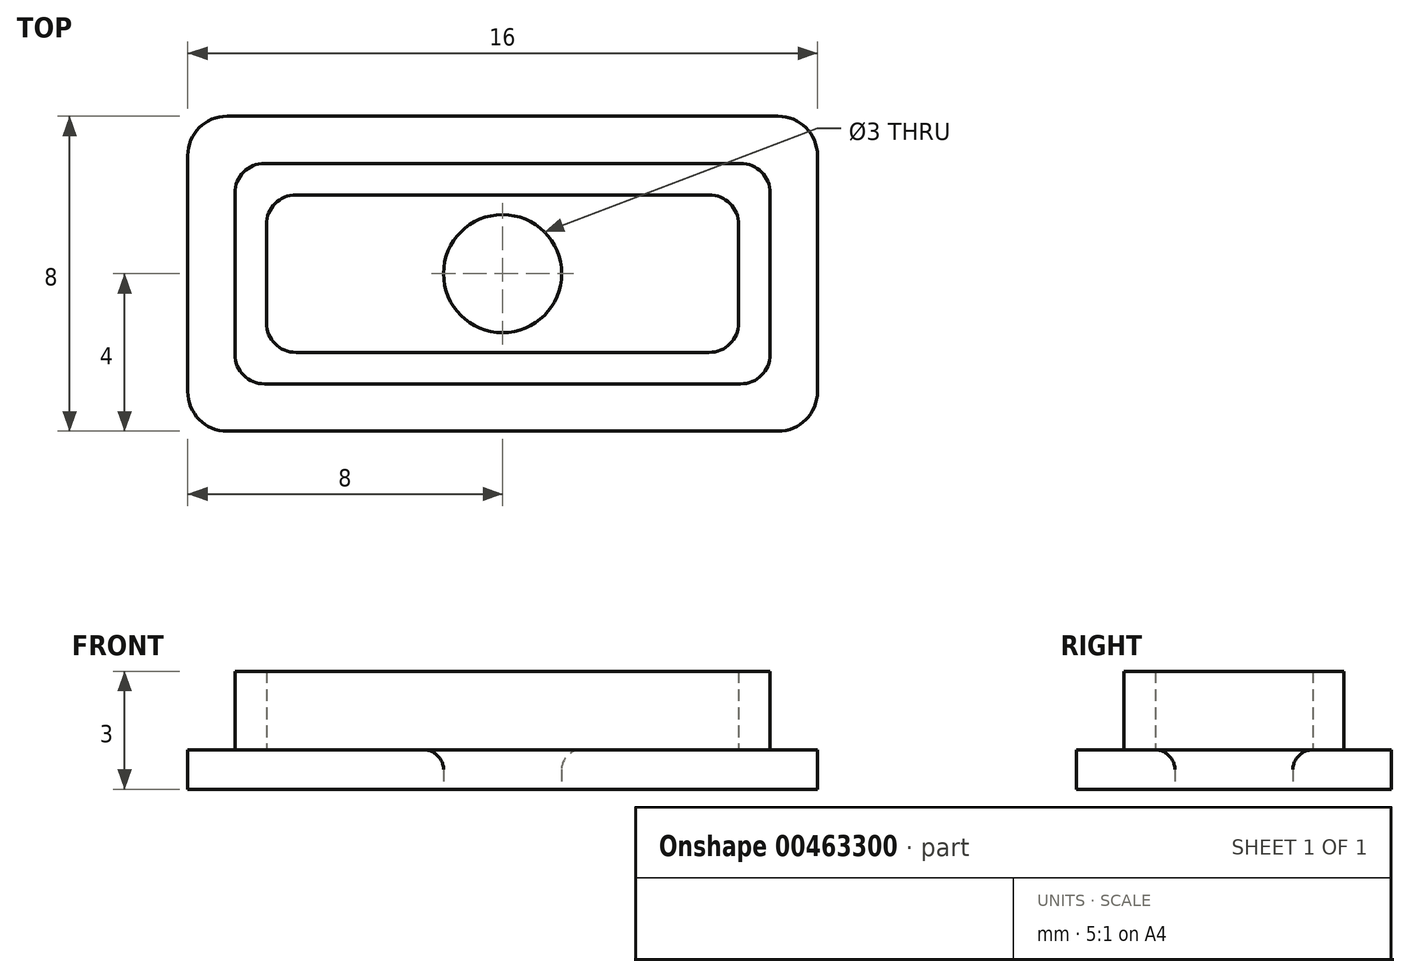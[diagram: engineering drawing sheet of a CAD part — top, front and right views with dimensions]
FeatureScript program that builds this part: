
annotation { "Feature Type Name" : "Feature", "Feature Type Description" : "" }
export const myFeature = defineFeature(function(context is Context, id is Id, definition is map)
    precondition{}
    {
        {
            var Q0;
            Q0=qCreatedBy(makeId("Top.planeOp"),FACE);
            var sketch = newSketch(context, id + "F0", { "sketchPlane" : qUnion([Q0])});
            skLineSegment(sketch, "E0.bottom", {"start": v(6.8, -2.8) * mm, "end": v(-6.8, -2.8) * mm});
            skLineSegment(sketch, "E0.top", {"start": v(6.8, 2.8) * mm, "end": v(-6.8, 2.8) * mm});
            skLineSegment(sketch, "E0.left", {"start": v(6.8, -2.8) * mm, "end": v(6.8, 2.8) * mm});
            skLineSegment(sketch, "E0.right", {"start": v(-6.8, -2.8) * mm, "end": v(-6.8, 2.8) * mm});
            skPoint(sketch, "E0.middle", {"position": v(0, 0) * mm});
            skSolve(sketch);
        }
        {
            var Q0;
            Q0 = qSketchRegion(id + "F0", true);
            extrude(context, id + "F1", {"entities" : qUnion([Q0]), "depth" : 3 * mm});
        }
        {
            var Q0;
            Q0=makeQuery(id+"F1.opExtrude","CAP_FACE",FACE,{"disambiguationData":[OSD([sQuery(id+"F0.wireOp",EDGE,"E0.bottom"),sQuery(id+"F0.wireOp",EDGE,"E0.top"),sQuery(id+"F0.wireOp",EDGE,"E0.left"),sQuery(id+"F0.wireOp",EDGE,"E0.right")])],"isStart":false});
            shell(context, id + "F2", {"entities" : qUnion([Q0]), "thickness" : 0.8 * mm});
        }
        {
            var Q0;
            Q0=qCreatedBy(makeId("Top.planeOp"),FACE);
            var sketch = newSketch(context, id + "F3", { "sketchPlane" : qUnion([Q0])});
            skLineSegment(sketch, "E1.bottom", {"start": v(8, -4) * mm, "end": v(-8, -4) * mm});
            skLineSegment(sketch, "E1.top", {"start": v(8, 4) * mm, "end": v(-8, 4) * mm});
            skLineSegment(sketch, "E1.left", {"start": v(8, -4) * mm, "end": v(8, 4) * mm});
            skLineSegment(sketch, "E1.right", {"start": v(-8, -4) * mm, "end": v(-8, 4) * mm});
            skPoint(sketch, "E1.middle", {"position": v(0, 0) * mm});
            skSolve(sketch);
        }
        {
            var Q0;
            Q0 = qSketchRegion(id + "F3", true);
            extrude(context, id + "F4", {"entities" : qUnion([Q0]), "operationType" : NewBodyOperationType.ADD, "depth" : 1 * mm});
        }
        {
            var Q0;
            Q0=makeQuery(id+"F1.opExtrude","SWEPT_EDGE",EDGE,{"disambiguationData":[OSD([sQuery(id+"F0.wireOp",EDGE,"E0.bottom"),sQuery(id+"F0.wireOp",EDGE,"E0.left")])]});
            var Q1;
            Q1=makeQuery(id+"F1.opExtrude","SWEPT_EDGE",EDGE,{"disambiguationData":[OSD([sQuery(id+"F0.wireOp",EDGE,"E0.top"),sQuery(id+"F0.wireOp",EDGE,"E0.left")])]});
            var Q2;
            Q2=makeQuery(id+"F2.opShell","OFFSET_EDGE",EDGE,{"disambiguationData":[OSD([sQuery(id+"F0.wireOp",EDGE,"E0.top"),sQuery(id+"F0.wireOp",EDGE,"E0.left")])]});
            var Q3;
            Q3=makeQuery(id+"F2.opShell","OFFSET_EDGE",EDGE,{"disambiguationData":[OSD([sQuery(id+"F0.wireOp",EDGE,"E0.bottom"),sQuery(id+"F0.wireOp",EDGE,"E0.left")])]});
            var Q4;
            Q4=makeQuery(id+"F2.opShell","OFFSET_EDGE",EDGE,{"disambiguationData":[OSD([sQuery(id+"F0.wireOp",EDGE,"E0.top"),sQuery(id+"F0.wireOp",EDGE,"E0.right")])]});
            var Q5;
            Q5=makeQuery(id+"F2.opShell","OFFSET_EDGE",EDGE,{"disambiguationData":[OSD([sQuery(id+"F0.wireOp",EDGE,"E0.bottom"),sQuery(id+"F0.wireOp",EDGE,"E0.right")])]});
            var Q6;
            Q6=makeQuery(id+"F1.opExtrude","SWEPT_EDGE",EDGE,{"disambiguationData":[OSD([sQuery(id+"F0.wireOp",EDGE,"E0.top"),sQuery(id+"F0.wireOp",EDGE,"E0.right")])]});
            var Q7;
            Q7=makeQuery(id+"F1.opExtrude","SWEPT_EDGE",EDGE,{"disambiguationData":[OSD([sQuery(id+"F0.wireOp",EDGE,"E0.bottom"),sQuery(id+"F0.wireOp",EDGE,"E0.right")])]});
            fillet(context, id + "F5", {"entities" : qUnion([Q0, Q1, Q2, Q3, Q4, Q5, Q6, Q7]), "radius" : 0.75 * mm, "allowEdgeOverflow" : false});
        }
        {
            var Q0;
            Q0=makeQuery(id+"F4.opExtrude","SWEPT_EDGE",EDGE,{"disambiguationData":[OSD([sQuery(id+"F3.wireOp",EDGE,"E1.bottom"),sQuery(id+"F3.wireOp",EDGE,"E1.right")])]});
            var Q1;
            Q1=makeQuery(id+"F4.opExtrude","SWEPT_EDGE",EDGE,{"disambiguationData":[OSD([sQuery(id+"F3.wireOp",EDGE,"E1.bottom"),sQuery(id+"F3.wireOp",EDGE,"E1.left")])]});
            var Q2;
            Q2=makeQuery(id+"F4.opExtrude","SWEPT_EDGE",EDGE,{"disambiguationData":[OSD([sQuery(id+"F3.wireOp",EDGE,"E1.top"),sQuery(id+"F3.wireOp",EDGE,"E1.left")])]});
            var Q3;
            Q3=makeQuery(id+"F4.opExtrude","SWEPT_EDGE",EDGE,{"disambiguationData":[OSD([sQuery(id+"F3.wireOp",EDGE,"E1.top"),sQuery(id+"F3.wireOp",EDGE,"E1.right")])]});
            fillet(context, id + "F6", {"entities" : qUnion([Q0, Q1, Q2, Q3]), "radius" : 1 * mm, "tangentPropagation" : true, "allowEdgeOverflow" : false});
        }
        {
            var Q0;
            Q0=qCreatedBy(makeId("Top.planeOp"),FACE);
            var sketch = newSketch(context, id + "F7", { "sketchPlane" : qUnion([Q0])});
            skCircle(sketch, "E2", {"center": v(0, 0) * mm, "radius": 1.5 * mm});
            skSolve(sketch);
        }
        {
            var Q0;
            Q0 = qSketchRegion(id + "F7", true);
            extrude(context, id + "F8", {"entities" : qUnion([Q0]), "depth" : 25 * mm});
        }
        {
            var Q0;
            Q0=makeQuery(id+"F8.opExtrude","SWEPT_BODY",BODY,{"disambiguationData":[OSD([sQuery(id+"F7.wireOp",EDGE,"E2")])]});
            var Q1;
            Q1=makeQuery(id+"F1.opExtrude","SWEPT_BODY",BODY,{"disambiguationData":[OSD([sQuery(id+"F0.wireOp",EDGE,"E0.bottom"),sQuery(id+"F0.wireOp",EDGE,"E0.top"),sQuery(id+"F0.wireOp",EDGE,"E0.left"),sQuery(id+"F0.wireOp",EDGE,"E0.right")])]});
            booleanBodies(context, id + "F9", {"operationType" : BooleanOperationType.SUBTRACTION, "tools" : qUnion([Q0]), "targets" : qUnion([Q1])});
        }
        {
            var Q0;
            Q0=makeQuery(id+"F9.opBoolean","INTERSECT",EDGE,{"derivedFrom":[makeQuery(id+"F4.boolean.opBoolean","SPLIT",FACE,{"disambiguationData":[TD([makeQuery(id+"F2.opShell","OFFSET_FACE",FACE,{"disambiguationData":[OSD([sQuery(id+"F0.wireOp",EDGE,"E0.bottom")])]})])],"derivedFrom":makeQuery(id+"F4.opExtrude","CAP_FACE",FACE,{"disambiguationData":[OSD([sQuery(id+"F3.wireOp",EDGE,"E1.bottom"),sQuery(id+"F3.wireOp",EDGE,"E1.top"),sQuery(id+"F3.wireOp",EDGE,"E1.left"),sQuery(id+"F3.wireOp",EDGE,"E1.right")])],"isStart":false})}),makeQuery(id+"F8.opExtrude","SWEPT_FACE",FACE,{"disambiguationData":[OSD([sQuery(id+"F7.wireOp",EDGE,"E2")])]})]});
            fillet(context, id + "F10", {"entities" : qUnion([Q0]), "radius" : 0.5 * mm, "tangentPropagation" : true, "allowEdgeOverflow" : false});
        }
    });
